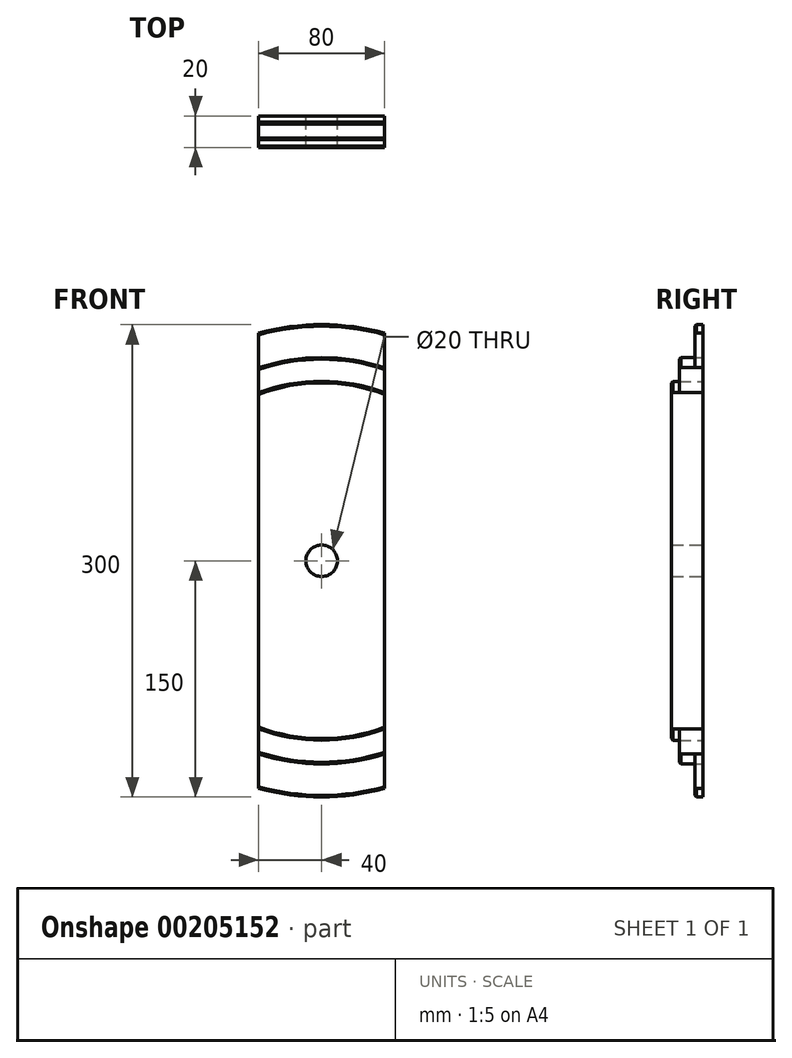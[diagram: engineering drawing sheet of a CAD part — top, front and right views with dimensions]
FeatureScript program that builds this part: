
annotation { "Feature Type Name" : "Feature", "Feature Type Description" : "" }
export const myFeature = defineFeature(function(context is Context, id is Id, definition is map)
    precondition{}
    {
        {
            var Q0;
            Q0=qCreatedBy(makeId("Front.planeOp"),FACE);
            var sketch = newSketch(context, id + "F0", { "sketchPlane" : qUnion([Q0])});
            skCircle(sketch, "E0", {"center": v(0, 0) * mm, "radius": 150 * mm});
            skCircle(sketch, "E1", {"center": v(0, 0) * mm, "radius": 129 * mm});
            skCircle(sketch, "E2", {"center": v(0, 0) * mm, "radius": 114 * mm});
            skLineSegment(sketch, "E3.bottom", {"start": v(-40, 155.75) * mm, "end": v(40, 155.75) * mm});
            skLineSegment(sketch, "E3.top", {"start": v(-40, -158.5) * mm, "end": v(40, -158.5) * mm});
            skLineSegment(sketch, "E3.left", {"start": v(-40, 155.75) * mm, "end": v(-40, -158.5) * mm});
            skLineSegment(sketch, "E3.right", {"start": v(40, 155.75) * mm, "end": v(40, -158.5) * mm});
            skCircle(sketch, "E4", {"center": v(0, 0) * mm, "radius": 10 * mm});
            skSolve(sketch);
        }
        {
            var Q0;
            {var subQ0=sQuery(id+"F0.wireOp",EDGE,"E3.left");var subQ1=sQuery(id+"F0.wireOp",EDGE,"E0");var subQ2=makeQuery(id+"F0.imprint","INTERSECT",VERTEX,{"disambiguationData":[OD(0.0)],"derivedFrom":[subQ1,subQ0]});Q0=makeQuery(id+"F0.imprint","IMPRINT",FACE,{"disambiguationData":[TD([[makeQuery(id+"F0.imprint","IMPRINT",EDGE,{"disambiguationData":[TD([[subQ2,1.0]])],"derivedFrom":subQ1}),1.0]])]});}
            var Q1;
            {var subQ0=sQuery(id+"F0.wireOp",EDGE,"E3.left");var subQ1=sQuery(id+"F0.wireOp",EDGE,"E0");var subQ2=makeQuery(id+"F0.imprint","INTERSECT",VERTEX,{"disambiguationData":[OD(1.0)],"derivedFrom":[subQ1,subQ0]});Q1=makeQuery(id+"F0.imprint","IMPRINT",FACE,{"disambiguationData":[TD([[makeQuery(id+"F0.imprint","IMPRINT",EDGE,{"disambiguationData":[TD([[subQ2,-1.0]])],"derivedFrom":subQ1}),1.0]])]});}
            extrude(context, id + "F1", {"entities" : qUnion([Q0, Q1]), "depth" : 5 * mm});
        }
        {
            var Q0;
            {var subQ0=sQuery(id+"F0.wireOp",EDGE,"E3.left");var subQ1=sQuery(id+"F0.wireOp",EDGE,"E1");var subQ2=makeQuery(id+"F0.imprint","INTERSECT",VERTEX,{"disambiguationData":[OD(1.0)],"derivedFrom":[subQ1,subQ0]});Q0=makeQuery(id+"F0.imprint","IMPRINT",FACE,{"disambiguationData":[TD([[makeQuery(id+"F0.imprint","IMPRINT",EDGE,{"disambiguationData":[TD([[subQ2,-1.0]])],"derivedFrom":subQ1}),1.0]])]});}
            var Q1;
            {var subQ0=sQuery(id+"F0.wireOp",EDGE,"E3.left");var subQ1=sQuery(id+"F0.wireOp",EDGE,"E1");var subQ2=makeQuery(id+"F0.imprint","INTERSECT",VERTEX,{"disambiguationData":[OD(0.0)],"derivedFrom":[subQ1,subQ0]});Q1=makeQuery(id+"F0.imprint","IMPRINT",FACE,{"disambiguationData":[TD([[makeQuery(id+"F0.imprint","IMPRINT",EDGE,{"disambiguationData":[TD([[subQ2,1.0]])],"derivedFrom":subQ1}),1.0]])]});}
            extrude(context, id + "F2", {"entities" : qUnion([Q0, Q1]), "depth" : 15 * mm});
        }
        {
            var Q0;
            {var subQ0=sQuery(id+"F0.wireOp",EDGE,"E3.left");var subQ1=sQuery(id+"F0.wireOp",EDGE,"E2");var subQ2=makeQuery(id+"F0.imprint","INTERSECT",VERTEX,{"disambiguationData":[OD(0.0)],"derivedFrom":[subQ1,subQ0]});Q0=makeQuery(id+"F0.imprint","IMPRINT",FACE,{"disambiguationData":[TD([[makeQuery(id+"F0.imprint","IMPRINT",EDGE,{"disambiguationData":[TD([[subQ2,1.0]])],"derivedFrom":subQ1}),1.0]])]});}
            extrude(context, id + "F3", {"entities" : qUnion([Q0]), "depth" : 20 * mm});
        }
        {
            var Q0;
            Q0=makeQuery(id+"F0.imprint","IMPRINT",FACE,{"disambiguationData":[TD([[makeQuery(id+"F0.imprint","IMPRINT",EDGE,{"derivedFrom":sQuery(id+"F0.wireOp",EDGE,"E4")}),1.0]])]});
            extrude(context, id + "F4", {"entities" : qUnion([Q0]), "operationType" : NewBodyOperationType.REMOVE, "depth" : 25 * mm});
        }
        {
            var Q0;
            {var subQ0=sQuery(id+"F0.wireOp",EDGE,"E0");Q0=makeQuery(id+"F1.opExtrude","CAP_EDGE",EDGE,{"disambiguationData":[OSD([subQ0]),TDD([makeQuery(id+"F0.imprint","IMPRINT",EDGE,{"disambiguationData":[TD([[makeQuery(id+"F0.imprint","INTERSECT",VERTEX,{"disambiguationData":[OD(0.0)],"derivedFrom":[subQ0,sQuery(id+"F0.wireOp",EDGE,"E3.left")]}),1.0]])],"derivedFrom":subQ0})])],"isStart":false});}
            var Q1;
            {var subQ0=sQuery(id+"F0.wireOp",EDGE,"E1");Q1=makeQuery(id+"F2.opExtrude","CAP_EDGE",EDGE,{"disambiguationData":[OSD([subQ0]),TDD([makeQuery(id+"F0.imprint","IMPRINT",EDGE,{"disambiguationData":[TD([[makeQuery(id+"F0.imprint","INTERSECT",VERTEX,{"disambiguationData":[OD(0.0)],"derivedFrom":[subQ0,sQuery(id+"F0.wireOp",EDGE,"E3.left")]}),1.0]])],"derivedFrom":subQ0})])],"isStart":false});}
            var Q2;
            {var subQ0=sQuery(id+"F0.wireOp",EDGE,"E2");Q2=makeQuery(id+"F3.opExtrude","CAP_EDGE",EDGE,{"disambiguationData":[OSD([subQ0]),TDD([makeQuery(id+"F0.imprint","IMPRINT",EDGE,{"disambiguationData":[TD([[makeQuery(id+"F0.imprint","INTERSECT",VERTEX,{"disambiguationData":[OD(0.0)],"derivedFrom":[subQ0,sQuery(id+"F0.wireOp",EDGE,"E3.left")]}),1.0]])],"derivedFrom":subQ0})])],"isStart":false});}
            var Q3;
            {var subQ0=sQuery(id+"F0.wireOp",EDGE,"E2");Q3=makeQuery(id+"F3.opExtrude","CAP_EDGE",EDGE,{"disambiguationData":[OSD([subQ0]),TDD([makeQuery(id+"F0.imprint","IMPRINT",EDGE,{"disambiguationData":[TD([[makeQuery(id+"F0.imprint","INTERSECT",VERTEX,{"disambiguationData":[OD(1.0)],"derivedFrom":[subQ0,sQuery(id+"F0.wireOp",EDGE,"E3.left")]}),-1.0]])],"derivedFrom":subQ0})])],"isStart":false});}
            var Q4;
            {var subQ0=sQuery(id+"F0.wireOp",EDGE,"E1");Q4=makeQuery(id+"F2.opExtrude","CAP_EDGE",EDGE,{"disambiguationData":[OSD([subQ0]),TDD([makeQuery(id+"F0.imprint","IMPRINT",EDGE,{"disambiguationData":[TD([[makeQuery(id+"F0.imprint","INTERSECT",VERTEX,{"disambiguationData":[OD(1.0)],"derivedFrom":[subQ0,sQuery(id+"F0.wireOp",EDGE,"E3.left")]}),-1.0]])],"derivedFrom":subQ0})])],"isStart":false});}
            var Q5;
            {var subQ0=sQuery(id+"F0.wireOp",EDGE,"E0");Q5=makeQuery(id+"F1.opExtrude","CAP_EDGE",EDGE,{"disambiguationData":[OSD([subQ0]),TDD([makeQuery(id+"F0.imprint","IMPRINT",EDGE,{"disambiguationData":[TD([[makeQuery(id+"F0.imprint","INTERSECT",VERTEX,{"disambiguationData":[OD(1.0)],"derivedFrom":[subQ0,sQuery(id+"F0.wireOp",EDGE,"E3.left")]}),-1.0]])],"derivedFrom":subQ0})])],"isStart":false});}
            chamfer(context, id + "F5", {"entities" : qUnion([Q0, Q1, Q2, Q3, Q4, Q5]), "width" : 1 * mm, "tangentPropagation" : true});
        }
    });
